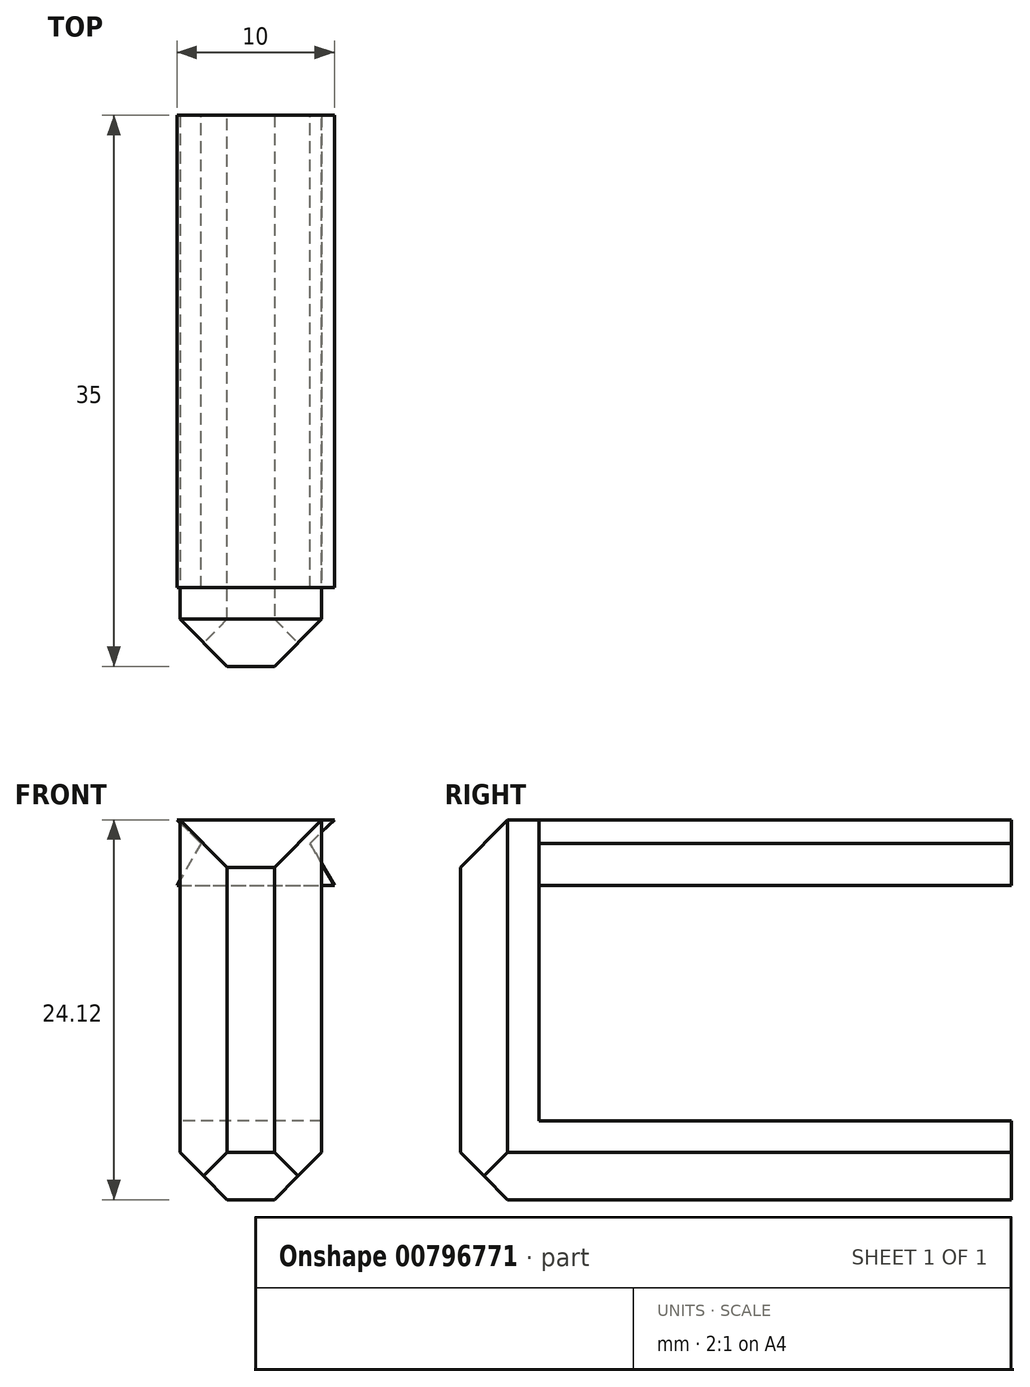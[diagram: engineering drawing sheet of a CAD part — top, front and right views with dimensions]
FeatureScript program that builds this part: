
annotation { "Feature Type Name" : "Feature", "Feature Type Description" : "" }
export const myFeature = defineFeature(function(context is Context, id is Id, definition is map)
    precondition{}
    {
        {
            var Q0;
            Q0=qCreatedBy(makeId("Front.planeOp"),FACE);
            var sketch = newSketch(context, id + "F0", { "sketchPlane" : qUnion([Q0])});
            skLineSegment(sketch, "E0", {"start": v(-4.7, 0.01) * mm, "end": v(5.3, 0.01) * mm});
            skLineSegment(sketch, "E1", {"start": v(-4.7, 0.01) * mm, "end": v(-3.16, -1.48) * mm});
            skLineSegment(sketch, "E2", {"start": v(-3.16, -1.48) * mm, "end": v(-4.7, -4.15) * mm});
            skLineSegment(sketch, "E3", {"start": v(-4.7, -4.15) * mm, "end": v(5.3, -4.15) * mm});
            skLineSegment(sketch, "E4", {"start": v(5.3, -4.15) * mm, "end": v(3.77, -1.48) * mm});
            skLineSegment(sketch, "E5", {"start": v(3.77, -1.48) * mm, "end": v(5.3, 0.01) * mm});
            skSolve(sketch);
        }
        {
            var Q0;
            Q0=makeQuery(id+"F0.imprint","IMPRINT",FACE,{"disambiguationData":[TD([[makeQuery(id+"F0.imprint","IMPRINT",EDGE,{"derivedFrom":sQuery(id+"F0.wireOp",EDGE,"E0")}),-1.0]])]});
            extrude(context, id + "F1", {"entities" : qUnion([Q0]), "depth" : 30 * mm, "offsetDistance" : 25.4 * mm});
        }
        {
            var Q0;
            Q0=qCreatedBy(makeId("Right.planeOp"),FACE);
            var sketch = newSketch(context, id + "F2", { "sketchPlane" : qUnion([Q0])});
            skLineSegment(sketch, "E6", {"start": v(-30, -3.9) * mm, "end": v(-30, -19.1) * mm});
            skLineSegment(sketch, "E7", {"start": v(0, -19.1) * mm, "end": v(-30, -19.1) * mm});
            skLineSegment(sketch, "E8", {"start": v(0, -19.1) * mm, "end": v(0, -24.1) * mm});
            skLineSegment(sketch, "E9", {"start": v(0, -24.1) * mm, "end": v(-35, -24.1) * mm});
            skLineSegment(sketch, "E10", {"start": v(-35, -24.1) * mm, "end": v(-35, 0) * mm});
            skLineSegment(sketch, "E11", {"start": v(-35, 0) * mm, "end": v(-30, 0) * mm});
            skLineSegment(sketch, "E12", {"start": v(-30, 0) * mm, "end": v(-30, -3.9) * mm});
            skSolve(sketch);
        }
        {
            var Q0;
            Q0=makeQuery(id+"F2.imprint","IMPRINT",FACE,{"disambiguationData":[TD([[makeQuery(id+"F2.imprint","IMPRINT",EDGE,{"derivedFrom":sQuery(id+"F2.wireOp",EDGE,"E6")}),-1.0]])]});
            extrude(context, id + "F3", {"entities" : qUnion([Q0]), "operationType" : NewBodyOperationType.ADD, "endBound" : BoundingType.SYMMETRIC, "depth" : 9 * mm, "offsetDistance" : 25.4 * mm});
        }
        {
            var Q0;
            Q0=makeQuery(id+"F3.opExtrude","SWEPT_EDGE",EDGE,{"disambiguationData":[OSD([sQuery(id+"F2.wireOp",EDGE,"E10"),sQuery(id+"F2.wireOp",EDGE,"E11")])]});
            var Q1;
            Q1=makeQuery(id+"F3.opExtrude","SWEPT_EDGE",EDGE,{"disambiguationData":[OSD([sQuery(id+"F2.wireOp",EDGE,"E9"),sQuery(id+"F2.wireOp",EDGE,"E10")])]});
            chamfer(context, id + "F4", {"entities" : qUnion([Q0, Q1]), "width" : 3 * mm, "tangentPropagation" : true});
        }
        {
            var Q0;
            Q0=makeQuery(id+"F3.opExtrude","CAP_EDGE",EDGE,{"disambiguationData":[OSD([sQuery(id+"F2.wireOp",EDGE,"E10")])],"isStart":true});
            var Q1;
            Q1=makeQuery(id+"F3.opExtrude","CAP_EDGE",EDGE,{"disambiguationData":[OSD([sQuery(id+"F2.wireOp",EDGE,"E10")])],"isStart":false});
            chamfer(context, id + "F5", {"entities" : qUnion([Q0, Q1]), "width" : 3 * mm, "tangentPropagation" : true});
        }
        {
            var Q0;
            Q0=makeQuery(id+"F3.opExtrude","CAP_EDGE",EDGE,{"disambiguationData":[OSD([sQuery(id+"F2.wireOp",EDGE,"E9")])],"isStart":true});
            var Q1;
            Q1=makeQuery(id+"F3.opExtrude","CAP_EDGE",EDGE,{"disambiguationData":[OSD([sQuery(id+"F2.wireOp",EDGE,"E9")])],"isStart":false});
            chamfer(context, id + "F6", {"entities" : qUnion([Q0, Q1]), "width" : 3 * mm, "tangentPropagation" : true});
        }
    });
